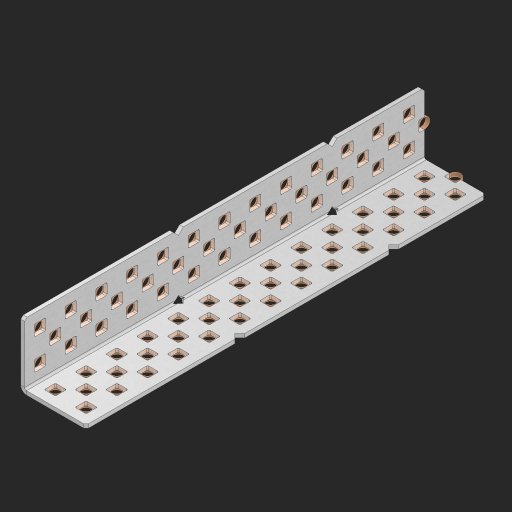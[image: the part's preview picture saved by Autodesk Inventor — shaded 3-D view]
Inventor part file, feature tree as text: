
AUTODESK INVENTOR PART (.ipt)
format: ipt  version: 2023 (Build 270158000, 158)  size: 1,162,752 bytes
history: native  units: in
note: dims shown in document units (in); Inventor stores cm internally (conversion verified against a paired STEP export)
features: other x84, extrude x76, sheet_metal_op x8, sketch x7, pattern_linear x2, mirror x1, chamfer x1
ambient origin geometry x8: Origin, YZ Plane, XZ Plane, XY Plane, X Axis, Y Axis, Z Axis, Center Point
bodies: Solid1 (feature_tree), Body (feature_tree)
feature tree (179):
  sheet_metal_op  "Flanges"
  sheet_metal_op  "Body Pattern"
  pattern_linear  "Center Pattern"  Spacing1=1.0in  [1 undecoded]
  other  "Arc Length"
  pattern_linear  "Notch Pattern"  Spacing1=0.25in  [1 undecoded]
  other  "Diagonal Plane"
  mirror  "Everything Mirrored"
  chamfer  "End Chamfer"
  sketch  "Sketch1"  dims[d0=1.0in]
  other  "Plate1"
  sketch  "Sketch2"  dims[d1=6.5in]
  other  "Plate2"
  sheet_metal_op  "Bend1"
  sheet_metal_op  "Corner1"
  sketch  "Sketch8"  dims[d2=0.0625in]
  sketch  "Sketch9"  dims[d3=0.0625in]
  other  "Srf91"
  sheet_metal_op  "Body Pattern Sketch"
  other  "Srf92"
  sketch  "Sketch13"  dims[d4=0.0312in]
  sketch  "Sketch15"  dims[d5=0.125in]
  sketch  "Sketch16"  dims[d6=0.0625in d7=1.0in d8=90.0deg d9=0.0312in d10=0.25in d11=0.0625in d12=0.0625in d49=0.182in d50=0.02in d52=0.25in d53=0.0625in d54=0.0in d55=0.172in d56=1.0in d57=0.0in d60=5.1181in d62=0.5in d63=0.7874in d65=0.5in d85=0.1473in d86=0.1782in d89=0.0625in d90=0.0in d91=0.04in d92=0.0491in d95=2.5in d96=0.04in d97=0.25in d98=45.0deg d99=0.25in d106=0.182in d107=0.02in d108=0.5in d110=0.0625in d111=0.0in d112=0.172in d113=0.5in d114=0.0in d117=0.5in d123=0.25in d125=0.25in d126=0.0491in d127=0.1473in d128=0.08in d129=0.04in d130=2.5in]
  other  "Srf786"
  other  "Srf856"
  other  "Srf857"
  other  "Srf858"
  other  "Srf859"
  other  "Srf860"
  other  "Srf861"
  other  "Srf889"
  other  "Srf890"
  other  "Srf891"
  other  "Srf1275"
  other  "Srf1276"
  other  "Srf1278"
  other  "Srf1279"
  other  "Srf1280"
  other  "Srf1281"
  other  "Srf1282"
  other  "Srf1283"
  other  "Srf1277"
  other  "Srf1285"
  other  "Srf1286"
  other  "Srf1287"
  other  "Srf1383"
  other  "Srf1384"
  other  "Srf1385"
  other  "Srf1386"
  other  "Srf1387"
  other  "Srf1388"
  other  "Srf1389"
  other  "Srf1390"
  other  "Srf1391"
  other  "Srf1392"
  other  "Srf1393"
  other  "Srf1394"
  other  "Srf1395"
  other  "Srf1396"
  other  "Srf1397"
  other  "Srf1398"
  other  "Srf1399"
  other  "Srf1400"
  other  "Srf1445"
  other  "Srf1446"
  other  "Srf1447"
  other  "Srf1448"
  other  "Srf1449"
  other  "Srf1450"
  other  "Srf1451"
  other  "Srf1452"
  other  "Srf1453"
  other  "Srf1475"
  other  "Srf1476"
  other  "Srf1477"
  other  "Srf1478"
  other  "Srf1479"
  other  "Srf1480"
  other  "Srf1481"
  other  "Srf1482"
  other  "Srf1483"
  other  "Srf1484"
  other  "Srf1485"
  other  "Srf1486"
  other  "Srf1487"
  other  "Srf1488"
  other  "Srf1489"
  other  "Srf1490"
  other  "Srf1491"
  other  "Srf1492"
  other  "Srf1537"
  other  "Srf1538"
  other  "Srf1539"
  other  "Srf1540"
  other  "Srf1541"
  other  "Srf1542"
  other  "Srf1543"
  other  "Srf1544"
  other  "Srf1545"
  sheet_metal_op  "Body Stamp"
  sheet_metal_op  "Body Circle"
  other  "Center Stamp"
  other  "Center Circle"
  sheet_metal_op  "Notch"
  extrude  "ExtrusionSrf92"  Depth=0.0625in
  extrude  "ExtrusionSrf856"  Depth=0.0625in
  extrude  "ExtrusionSrf857"  Depth=0.182in
  extrude  "ExtrusionSrf858"  Depth=0.02in
  extrude  "ExtrusionSrf859"  Depth=0.25in
  extrude  "ExtrusionSrf860"  Depth=0.0625in
  extrude  "ExtrusionSrf861"  TaperAngle=0.0deg  [1 undecoded]
  extrude  "ExtrusionSrf889"  Depth=2.5in
  extrude  "ExtrusionSrf890"  Depth=1.0in TaperAngle=0.0deg
  extrude  "ExtrusionSrf891"  Depth=2.5in
  extrude  "ExtrusionSrf1275"  Depth=0.5in
  extrude  "ExtrusionSrf1276"  Depth=2.5in
  extrude  "ExtrusionSrf1277"  Depth=2.5in
  extrude  "ExtrusionSrf1278"  Depth=0.0625in
  extrude  "ExtrusionSrf1279"  Depth=2.5in TaperAngle=0.0deg
  extrude  "ExtrusionSrf1280"  Depth=2.5in
  extrude  "ExtrusionSrf1281"  Depth=0.25in TaperAngle=45.0deg
  extrude  "ExtrusionSrf1282"  Depth=0.25in
  extrude  "ExtrusionSrf1345"  Depth=0.182in
  extrude  "ExtrusionSrf1346"  Depth=0.02in
  extrude  "ExtrusionSrf1347"  Depth=0.5in
  extrude  "ExtrusionSrf1348"  Depth=0.0625in
  extrude  "ExtrusionSrf1383"  TaperAngle=0.0deg  [1 undecoded]
  extrude  "ExtrusionSrf1384"  Depth=2.5in
  extrude  "ExtrusionSrf1385"  Depth=0.5in TaperAngle=0.0deg
  extrude  "ExtrusionSrf1386"  Depth=0.5in
  extrude  "ExtrusionSrf1387"  Depth=0.25in
  extrude  "ExtrusionSrf1388"  Depth=0.25in
  extrude  "ExtrusionSrf1389"  Depth=2.5in
  extrude  "ExtrusionSrf1390"  Depth=2.5in
  extrude  "ExtrusionSrf1391"  Depth=2.5in
  extrude  "ExtrusionSrf1392"  Depth=2.5in
  extrude  "ExtrusionSrf1393"  Depth=2.5in
  extrude  "ExtrusionSrf1394"  [1 undecoded]
  extrude  "ExtrusionSrf1395"  [1 undecoded]
  extrude  "ExtrusionSrf1396"  [1 undecoded]
  extrude  "ExtrusionSrf1397"  [1 undecoded]
  extrude  "ExtrusionSrf1398"  [1 undecoded]
  extrude  "ExtrusionSrf1399"  [1 undecoded]
  extrude  "ExtrusionSrf1400"  [1 undecoded]
  extrude  "ExtrusionSrf1445"  [1 undecoded]
  extrude  "ExtrusionSrf1446"  [1 undecoded]
  extrude  "ExtrusionSrf1447"  [1 undecoded]
  extrude  "ExtrusionSrf1448"  [1 undecoded]
  extrude  "ExtrusionSrf1449"  [1 undecoded]
  extrude  "ExtrusionSrf1450"  [1 undecoded]
  extrude  "ExtrusionSrf1451"  [1 undecoded]
  extrude  "ExtrusionSrf1452"  [1 undecoded]
  extrude  "ExtrusionSrf1453"  [1 undecoded]
  extrude  "ExtrusionSrf1475"  [1 undecoded]
  extrude  "ExtrusionSrf1476"  [1 undecoded]
  extrude  "ExtrusionSrf1477"  [1 undecoded]
  extrude  "ExtrusionSrf1478"  [1 undecoded]
  extrude  "ExtrusionSrf1479"  [1 undecoded]
  extrude  "ExtrusionSrf1480"  [1 undecoded]
  extrude  "ExtrusionSrf1481"  [1 undecoded]
  extrude  "ExtrusionSrf1482"  [1 undecoded]
  extrude  "ExtrusionSrf1483"  [1 undecoded]
  extrude  "ExtrusionSrf1484"  [1 undecoded]
  extrude  "ExtrusionSrf1485"  [1 undecoded]
  extrude  "ExtrusionSrf1486"  [1 undecoded]
  extrude  "ExtrusionSrf1487"  [1 undecoded]
  extrude  "ExtrusionSrf1488"  [1 undecoded]
  extrude  "ExtrusionSrf1489"  [1 undecoded]
  extrude  "ExtrusionSrf1490"  [1 undecoded]
  extrude  "ExtrusionSrf1491"  [1 undecoded]
  extrude  "ExtrusionSrf1492"  [1 undecoded]
  extrude  "ExtrusionSrf1537"  [1 undecoded]
  extrude  "ExtrusionSrf1538"  [1 undecoded]
  extrude  "ExtrusionSrf1539"  [1 undecoded]
  extrude  "ExtrusionSrf1540"  [1 undecoded]
  extrude  "ExtrusionSrf1541"  [1 undecoded]
  extrude  "ExtrusionSrf1542"  [1 undecoded]
  extrude  "ExtrusionSrf1543"  [1 undecoded]
  extrude  "ExtrusionSrf1544"  [1 undecoded]
  extrude  "ExtrusionSrf1545"  [1 undecoded]
note: 47 required parameter values undecoded (feature->parameter linkage not recoverable at this tier; creation-order binding heuristic only, values carry confidence <= 0.55)
